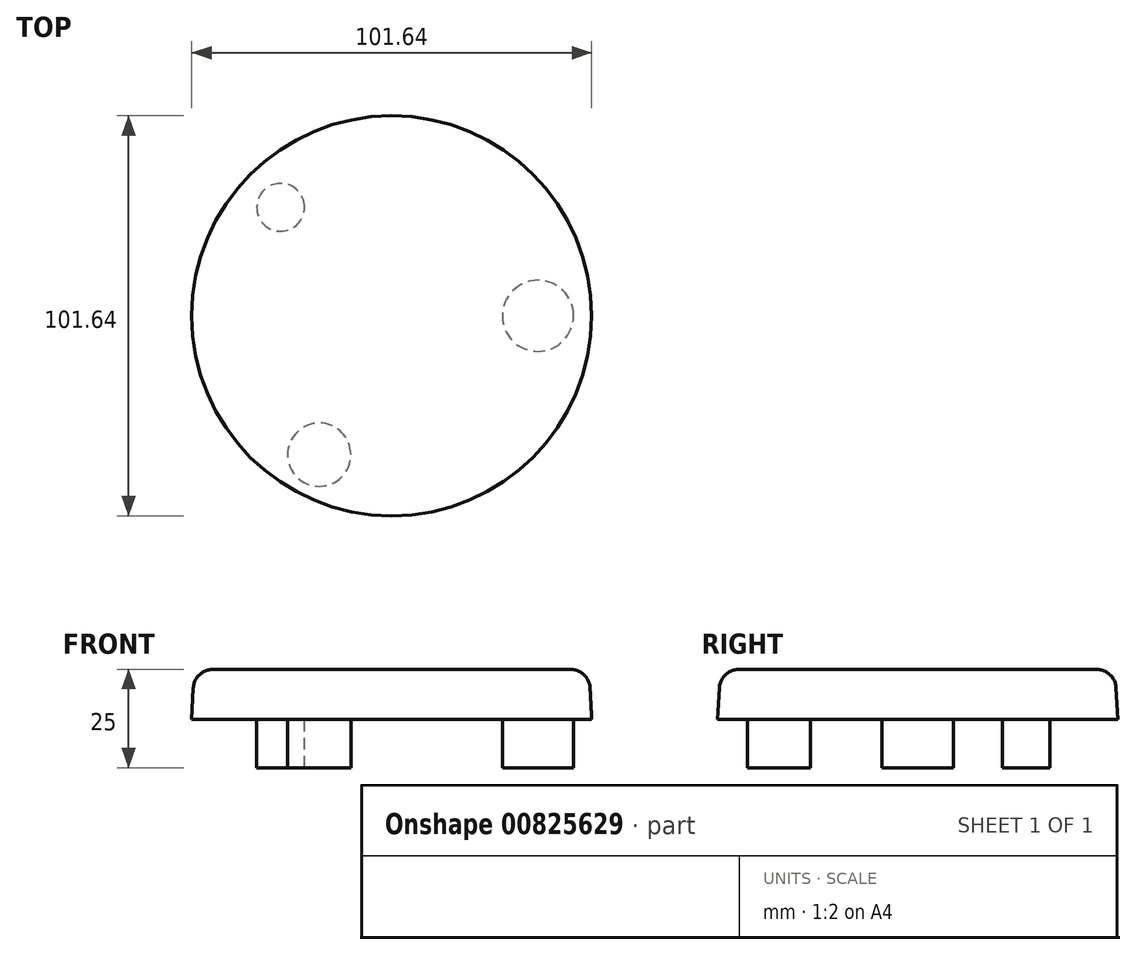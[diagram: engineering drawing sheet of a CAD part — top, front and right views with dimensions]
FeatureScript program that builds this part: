
annotation { "Feature Type Name" : "Feature", "Feature Type Description" : "" }
export const myFeature = defineFeature(function(context is Context, id is Id, definition is map)
    precondition{}
    {
        {
            var Q0;
            Q0=qCreatedBy(makeId("Top.planeOp"),FACE);
            var sketch = newSketch(context, id + "F0", { "sketchPlane" : qUnion([Q0])});
            skCircle(sketch, "E0", {"center": v(0, 0) * mm, "radius": 50.82 * mm});
            skSolve(sketch);
        }
        {
            var Q0;
            Q0=makeQuery(id+"F0.imprint","IMPRINT",FACE,{"disambiguationData":[TD([[makeQuery(id+"F0.imprint","IMPRINT",EDGE,{"derivedFrom":sQuery(id+"F0.wireOp",EDGE,"E0")}),1.0]])]});
            extrude(context, id + "F1", {"entities" : qUnion([Q0]), "depth" : 12.7 * mm, "offsetDistance" : 25.4 * mm, "hasDraft" : true, "draftAngle" : 3 * degree, "draftPullDirection" : true});
        }
        {
            var Q0;
            Q0=makeQuery(id+"F1.opExtrude","CAP_FACE",FACE,{"disambiguationData":[OSD([sQuery(id+"F0.wireOp",EDGE,"E0")])],"isStart":false});
            var sketch = newSketch(context, id + "F2", { "sketchPlane" : qUnion([Q0])});
            skLineSegment(sketch, "E1", {"start": v(0, 0) * mm, "end": v(37.15, 0) * mm});
            skLineSegment(sketch, "E2", {"start": v(0, 0) * mm, "end": v(-28.2, 27.55) * mm});
            skLineSegment(sketch, "E3", {"start": v(0, 0) * mm, "end": v(-18.4, -35.28) * mm});
            skCircle(sketch, "E4", {"center": v(-18.4, -35.28) * mm, "radius": 8.04 * mm});
            skCircle(sketch, "E5", {"center": v(-28.2, 27.55) * mm, "radius": 6.08 * mm});
            skCircle(sketch, "E6", {"center": v(37.15, 0) * mm, "radius": 9.04 * mm});
            skSolve(sketch);
        }
        {
            var Q0;
            Q0=makeQuery(id+"F2.imprint","IMPRINT",FACE,{"disambiguationData":[TD([[makeQuery(id+"F2.imprint","IMPRINT",EDGE,{"derivedFrom":sQuery(id+"F2.wireOp",EDGE,"E4")}),1.0]])]});
            var Q1;
            Q1=makeQuery(id+"F2.imprint","IMPRINT",FACE,{"disambiguationData":[TD([[makeQuery(id+"F2.imprint","IMPRINT",EDGE,{"derivedFrom":sQuery(id+"F2.wireOp",EDGE,"E6")}),1.0]])]});
            var Q2;
            Q2=makeQuery(id+"F2.imprint","IMPRINT",FACE,{"disambiguationData":[TD([[makeQuery(id+"F2.imprint","IMPRINT",EDGE,{"derivedFrom":sQuery(id+"F2.wireOp",EDGE,"E5")}),1.0]])]});
            extrude(context, id + "F3", {"entities" : qUnion([Q0, Q1, Q2]), "operationType" : NewBodyOperationType.ADD, "oppositeDirection" : true, "depth" : 25 * mm, "offsetDistance" : 25 * mm});
        }
        {
            var Q0;
            Q0=makeQuery(id+"F1.opExtrude","CAP_EDGE",EDGE,{"disambiguationData":[OSD([sQuery(id+"F0.wireOp",EDGE,"E0")])],"isStart":false});
            fillet(context, id + "F4", {"entities" : qUnion([Q0]), "radius" : 5 * mm, "tangentPropagation" : true, "allowEdgeOverflow" : false});
        }
    });
